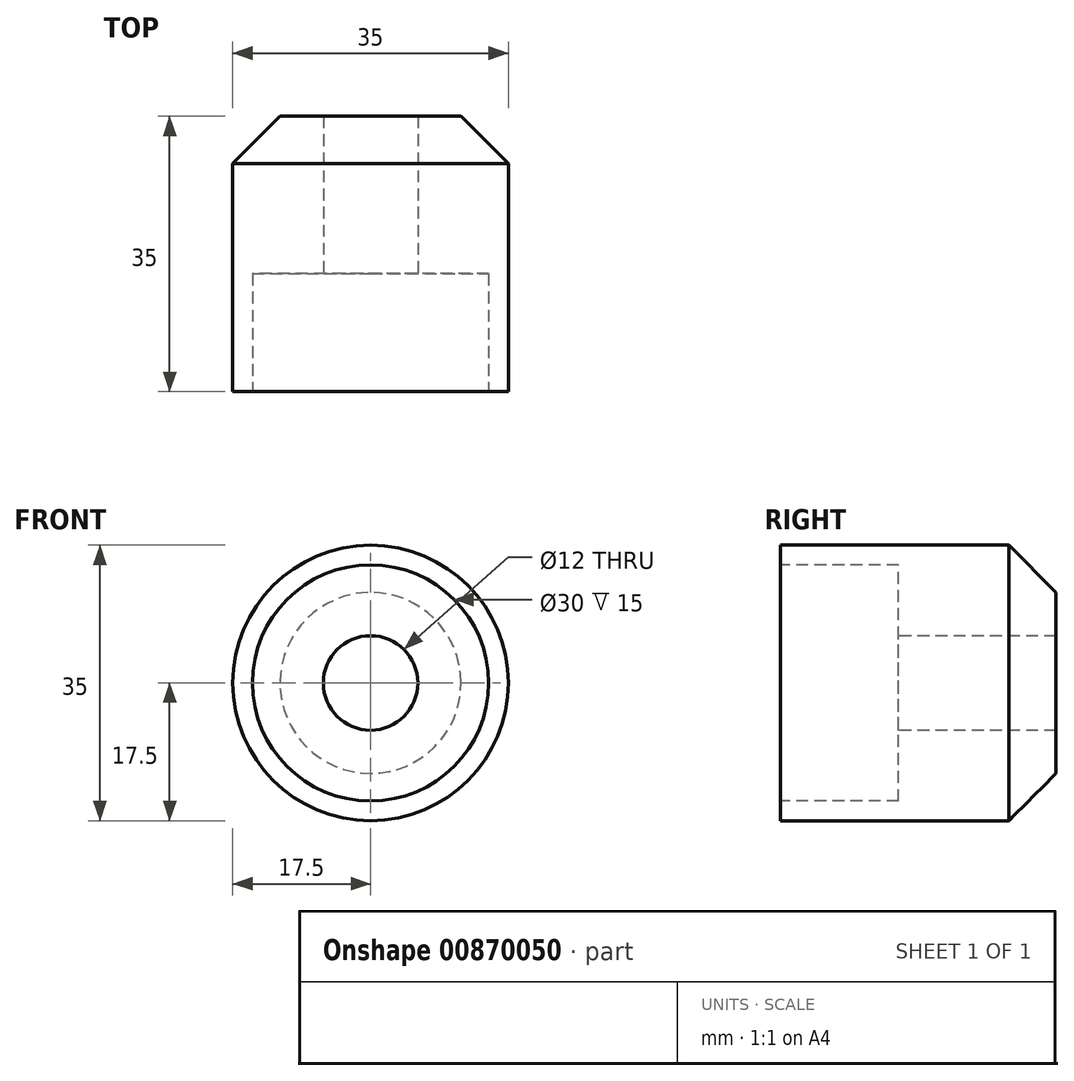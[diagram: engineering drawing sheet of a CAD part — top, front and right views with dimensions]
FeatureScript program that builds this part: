
annotation { "Feature Type Name" : "Feature", "Feature Type Description" : "" }
export const myFeature = defineFeature(function(context is Context, id is Id, definition is map)
    precondition{}
    {
        {
            var Q0;
            Q0=qCreatedBy(makeId("Right.planeOp"),FACE);
            var sketch = newSketch(context, id + "F0", { "sketchPlane" : qUnion([Q0])});
            skLineSegment(sketch, "E0", {"start": v(0, 0) * mm, "end": v(15, 0) * mm, "construction": true});
            skLineSegment(sketch, "E1", {"start": v(35, 6) * mm, "end": v(35, 17.5) * mm});
            skLineSegment(sketch, "E2", {"start": v(35, 17.5) * mm, "end": v(0, 17.5) * mm});
            skLineSegment(sketch, "E3", {"start": v(0, 17.5) * mm, "end": v(0, 15) * mm});
            skLineSegment(sketch, "E4", {"start": v(0, 15) * mm, "end": v(15, 15) * mm});
            skLineSegment(sketch, "E5", {"start": v(15, 15) * mm, "end": v(15, 6) * mm});
            skLineSegment(sketch, "E6", {"start": v(15, 6) * mm, "end": v(35, 6) * mm});
            skSolve(sketch);
        }
        {
            var Q0;
            Q0 = qSketchRegion(id + "F0", true);
            var Q1;
            Q1=sQuery(id+"F0.wireOp",EDGE,"E0");
            revolve(context, id + "F1", {"surfaceOperationType" : NewSurfaceOperationType.NEW, "entities" : qUnion([Q0]), "axis" : qUnion([Q1]), "revolveType" : RevolveType.FULL});
        }
        {
            var Q0;
            Q0=makeQuery(id+"F1.opRevolve","SWEPT_EDGE",EDGE,{"disambiguationData":[OSD([sQuery(id+"F0.wireOp",EDGE,"E1"),sQuery(id+"F0.wireOp",EDGE,"E2")])]});
            chamfer(context, id + "F2", {"entities" : qUnion([Q0]), "width" : 6 * mm, "tangentPropagation" : true});
        }
    });
